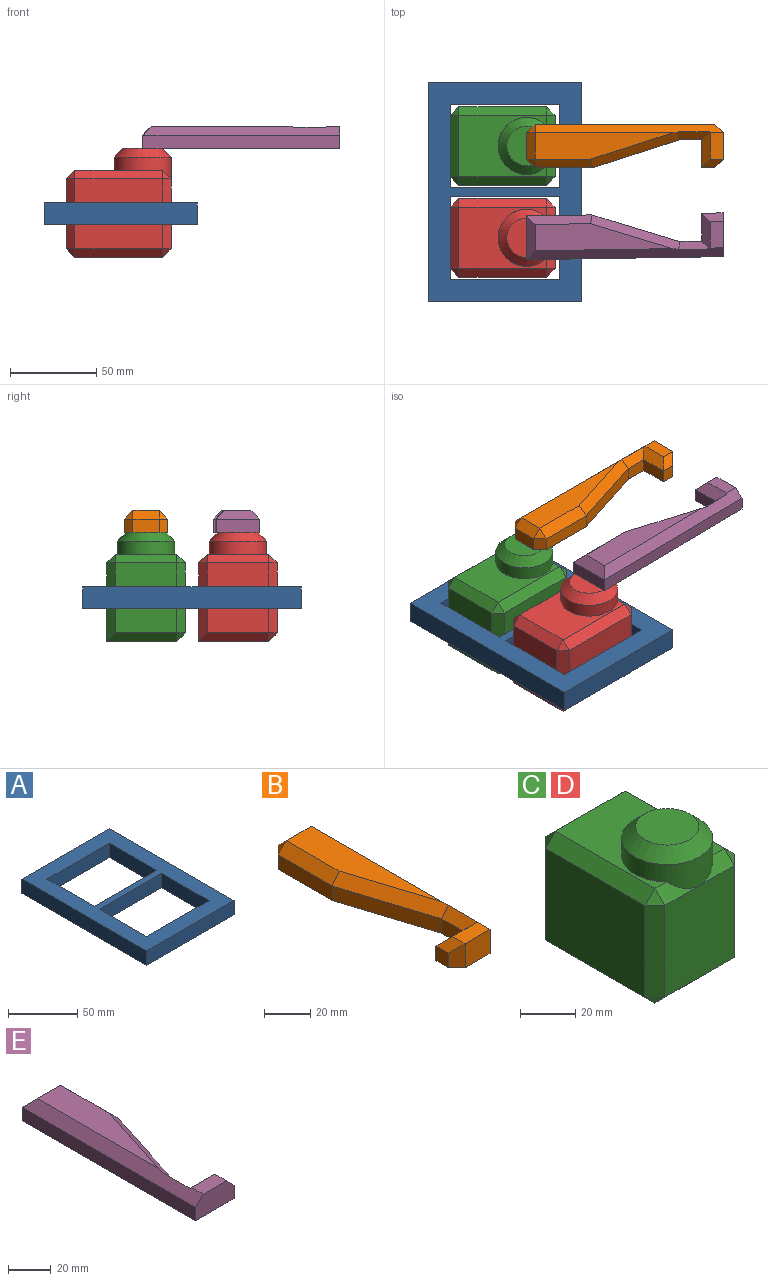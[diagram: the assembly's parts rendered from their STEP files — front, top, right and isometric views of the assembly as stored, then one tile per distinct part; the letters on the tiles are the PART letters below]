
ASSEMBLY  parts=5 mates=4
PART A: 14 faces, bbox 88.9x127x12.7 mm
  f0: plane 127x12.7mm, normal (-1,0,0), area 1612.9mm2, adj f1,f11,f12,f13
  f1: plane 88.9x12.7mm, normal (0,-1,0), area 1129mm2, adj f0,f2,f12,f13
  f2: plane 127x12.7mm, normal (1,0,0), area 1612.9mm2, adj f1,f11,f12,f13
  f3: plane 48.26x12.7mm, normal (-1,0,0), area 612.9mm2, adj f4,f9,f12,f13
  f4: plane 63.5x12.7mm, normal (0,1,0), area 806.5mm2, adj f3,f5,f12,f13
  f5: plane 48.26x12.7mm, normal (1,0,0), area 612.9mm2, adj f4,f9,f12,f13
  f6: plane 63.5x12.7mm, normal (0,-1,0), area 806.5mm2, adj f7,f10,f12,f13
  f7: plane 48.26x12.7mm, normal (-1,0,0), area 612.9mm2, adj f6,f8,f12,f13
  f8: plane 63.5x12.7mm, normal (0,1,0), area 806.5mm2, adj f7,f10,f12,f13
  f9: plane 63.5x12.7mm, normal (0,-1,0), area 806.5mm2, adj f3,f5,f12,f13
  f10: plane 48.26x12.7mm, normal (1,0,0), area 612.9mm2, adj f6,f8,f12,f13
  f11: plane 88.9x12.7mm, normal (0,1,0), area 1129mm2, adj f0,f2,f12,f13
  f12: plane 127x88.9mm, normal (0,0,1), area 5161.3mm2, adj f0,f1,f2,f3,f4,f5,f6,f7
  f13: plane 127x88.9mm, normal (0,0,-1), area 5161.3mm2, adj f0,f1,f2,f3,f4,f5,f6,f7
PART B: 24 faces, bbox 25.4x114.3x12.7 mm
  f0: plane 15.24x7.62mm, normal (0,0,1), area 116.1mm2, adj f6,f20,f21,f22
  f1: plane 33.02x7.62mm, normal (-1,0,0), area 251.6mm2, adj f2,f10,f11,f13
  f2: plane 50.8x16.26mm, normal (-0.95,-0.3,0), area 406.5mm2, adj f1,f3,f10,f16
  f3: plane 12.7x7.62mm, normal (-1,0,0), area 96.8mm2, adj f2,f4,f10,f19
  f4: plane 16.26x7.62mm, normal (0,1,0), area 123.9mm2, adj f3,f5,f10,f21
  f5: plane 7.62x7.62mm, normal (-1,0,0), area 58.1mm2, adj f4,f10,f22,f23
  f6: plane 15.24x12.7mm, normal (0,-1,0), area 193.5mm2, adj f0,f10,f18,f23
  f7: plane 104.14x7.62mm, normal (1,0,0), area 793.5mm2, adj f10,f15,f18,f20
  f8: plane 15.24x7.62mm, normal (0,1,0), area 116.1mm2, adj f10,f11,f14,f15
  f9: plane 79.83x15.24mm, normal (0,0,1), area 853.9mm2, adj f13,f14,f16,f20
  f10: plane 114.3x25.4mm, normal (0,0,-1), area 2232mm2, adj f1,f2,f3,f4,f5,f6,f7,f8
  f11: plane 7.62x5.08mm, normal (-0.71,0.71,0), area 54.7mm2, adj f1,f8,f10,f12
  f12: plane 5.08x5.08mm, normal (-0.58,0.58,0.58), area 22.3mm2, adj f11,f13,f14
  f13: plane 33.02x5.08mm, normal (-0.71,0,0.71), area 234.4mm2, adj f1,f9,f12,f16
  f14: plane 15.24x5.08mm, normal (0,0.71,0.71), area 109.5mm2, adj f8,f9,f12,f17
  f15: plane 7.62x5.08mm, normal (0.71,0.71,0), area 54.7mm2, adj f7,f8,f10,f17
  f16: plane 51.59x20.83mm, normal (-0.67,-0.22,0.71), area 382mm2, adj f2,f9,f13,f19,f20
  f17: plane 5.08x5.08mm, normal (0.58,0.58,0.58), area 22.3mm2, adj f14,f15,f20
  f18: plane 12.7x5.08mm, normal (0.71,-0.71,0), area 73mm2, adj f6,f7,f10,f20
  f19: plane 17.98x4.57mm, normal (-0.71,0,0.71), area 99.1mm2, adj f3,f16,f20,f21
  f20: plane 109.22x5.08mm, normal (0.71,0,0.71), area 752mm2, adj f0,f7,f9,f16,f17,f18,f19,f21
  f21: plane 20.83x5.08mm, normal (0,0.71,0.71), area 116.5mm2, adj f0,f4,f19,f20,f22
  f22: plane 12.7x5.08mm, normal (-0.71,0,0.71), area 54.7mm2, adj f0,f5,f21,f23
  f23: plane 12.7x5.08mm, normal (-0.71,-0.71,0), area 73mm2, adj f5,f6,f10,f22
PART C: 27 faces, bbox 45.7x61x63.5 mm
  f0: plane 40.64x35.56mm, normal (0,-1,0), area 1445.2mm2, adj f12,f17,f21,f23,f25
  f1: plane 50.8x45.72mm, normal (1,0,0), area 2322.6mm2, adj f5,f9,f16,f17
  f2: plane 40.64x35.56mm, normal (0,1,0), area 1445.2mm2, adj f8,f9,f14,f15
  f3: plane 50.8x40.64mm, normal (-1,0,0), area 2064.5mm2, adj f13,f14,f21,f22
  f4: plane 50.8x35.56mm, normal (0,0,1), area 1029.1mm2, adj f6,f15,f16,f22,f23,f25
  f5: plane 50.8x40.64mm, normal (0,0,-1), area 2064.5mm2, adj f1,f8,f12,f13
  f6: cylinder r=16.56mm len=33.11mm, axis (0,0,-1), area 881.9mm2, adj f4,f23,f25,f26
  f7: plane 22.95x22.95mm, normal (0,0,1), area 413.7mm2, adj f26
  f8: plane 40.64x5.08mm, normal (0,0.71,-0.71), area 273.7mm2, adj f2,f5,f9,f10
  f9: plane 45.72x5.08mm, normal (0.71,0.71,0), area 310.2mm2, adj f1,f2,f8,f11
  f10: plane 5.08x5.08mm, normal (-0.58,0.58,-0.58), area 22.3mm2, adj f8,f13,f14
  f11: plane 5.08x5.08mm, normal (0.58,0.58,0.58), area 22.3mm2, adj f9,f15,f16
  f12: plane 40.64x5.08mm, normal (0,-0.71,-0.71), area 273.7mm2, adj f0,f5,f17,f18
  f13: plane 50.8x5.08mm, normal (-0.71,0,-0.71), area 365mm2, adj f3,f5,f10,f18
  f14: plane 40.64x5.08mm, normal (-0.71,0.71,0), area 292mm2, adj f2,f3,f10,f19
  f15: plane 35.56x5.08mm, normal (0,0.71,0.71), area 255.5mm2, adj f2,f4,f11,f19
  f16: plane 50.8x5.08mm, normal (0.71,0,0.71), area 365mm2, adj f1,f4,f11,f20
  f17: plane 45.72x5.08mm, normal (0.71,-0.71,0), area 310.2mm2, adj f0,f1,f12,f20
  f18: plane 5.08x5.08mm, normal (-0.58,-0.58,-0.58), area 22.3mm2, adj f12,f13,f21
  f19: plane 5.08x5.08mm, normal (-0.58,0.58,0.58), area 22.3mm2, adj f14,f15,f22
  f20: plane 5.08x5.08mm, normal (0.58,-0.58,0.58), area 22.3mm2, adj f16,f17,f23
  f21: plane 40.64x5.08mm, normal (-0.71,-0.71,0), area 292mm2, adj f0,f3,f18,f24
  f22: plane 50.8x5.08mm, normal (-0.71,0,0.71), area 365mm2, adj f3,f4,f19,f24
  f23: plane 17.78x5.08mm, normal (0,-0.71,0.71), area 68.6mm2, adj f0,f4,f6,f20
  f24: plane 5.08x5.08mm, normal (-0.58,-0.58,0.58), area 22.3mm2, adj f21,f22,f25
  f25: plane 17.78x5.08mm, normal (0,-0.71,0.71), area 68.6mm2, adj f0,f4,f6,f24
  f26: cone r=11.48mm half-angle=45deg, axis (0,0,-1), area 632.6mm2, adj f6,f7
PART D: same geometry as C
PART E: 18 faces, bbox 25.4x114.3x12.7 mm
  f0: plane 79.83x15.24mm, normal (0,0,1), area 853.9mm2, adj f12,f15,f16,f17
  f1: plane 114.3x7.62mm, normal (-1,0,0), area 871mm2, adj f2,f8,f10,f16
  f2: plane 25.4x12.7mm, normal (0,-1,0), area 296.8mm2, adj f1,f3,f9,f10,f11,f16
  f3: plane 12.7x7.62mm, normal (1,0,0), area 96.8mm2, adj f2,f4,f10,f11
  f4: plane 16.26x7.62mm, normal (0,1,0), area 123.9mm2, adj f3,f5,f10,f14
  f5: plane 12.7x7.62mm, normal (1,0,0), area 96.8mm2, adj f4,f6,f10,f13
  f6: plane 50.8x16.26mm, normal (0.95,-0.3,0), area 406.5mm2, adj f5,f7,f10,f12
  f7: plane 38.1x7.62mm, normal (1,0,0), area 290.3mm2, adj f6,f8,f10,f15
  f8: plane 25.4x7.62mm, normal (0,1,0), area 193.5mm2, adj f1,f7,f10,f17
  f9: plane 15.24x7.62mm, normal (0,0,1), area 116.1mm2, adj f2,f11,f14,f16
  f10: plane 114.3x25.4mm, normal (0,0,-1), area 2283.6mm2, adj f1,f2,f3,f4,f5,f6,f7,f8
  f11: plane 12.7x5.08mm, normal (0.71,0,0.71), area 73mm2, adj f2,f3,f9,f14
  f12: plane 51.59x20.83mm, normal (0.67,-0.22,0.71), area 382mm2, adj f0,f6,f13,f15,f16
  f13: plane 17.98x4.57mm, normal (0.71,0,0.71), area 99.1mm2, adj f5,f12,f14,f16
  f14: plane 20.83x5.08mm, normal (0,0.71,0.71), area 116.5mm2, adj f4,f9,f11,f13,f16
  f15: plane 38.1x5.08mm, normal (0.71,0,0.71), area 252.6mm2, adj f0,f7,f12,f17
  f16: plane 114.3x5.08mm, normal (-0.71,0,0.71), area 788.5mm2, adj f0,f1,f2,f9,f12,f13,f14,f17
  f17: plane 25.4x5.08mm, normal (0,0.71,0.71), area 146mm2, adj f0,f8,f15,f16
PLACE A t=(-45.23,7.55,8.54)mm fixed
PLACE B rot(axis=(0,0,1),90deg) t=(-41.19,-90.55,52.99)mm
PLACE C rot(axis=(0,0,1),90deg) t=(-77.9,-46.59,-10.51)mm
PLACE D rot(axis=(0,0,1),90deg) t=(-77.9,-99.93,-10.51)mm
PLACE E rot(axis=(0,0,1),90.9deg) t=(-16.07,-225.52,52.99)mm
MATE fastened B.f10 <-> C.f6  axis (0,0,-1) through (-57.97,17.7,52.99)mm
MATE revolute E.f10 <-> D.f6  axis (0,0,-1) through (-57.97,-35.64,52.99)mm
MATE fastened C.f2 <-> A.f10  axis (-1,0,0) through (-102.38,17.7,14.89)mm
MATE fastened D.f2 <-> A.f5  axis (-1,0,0) through (-102.38,-35.64,14.89)mm
